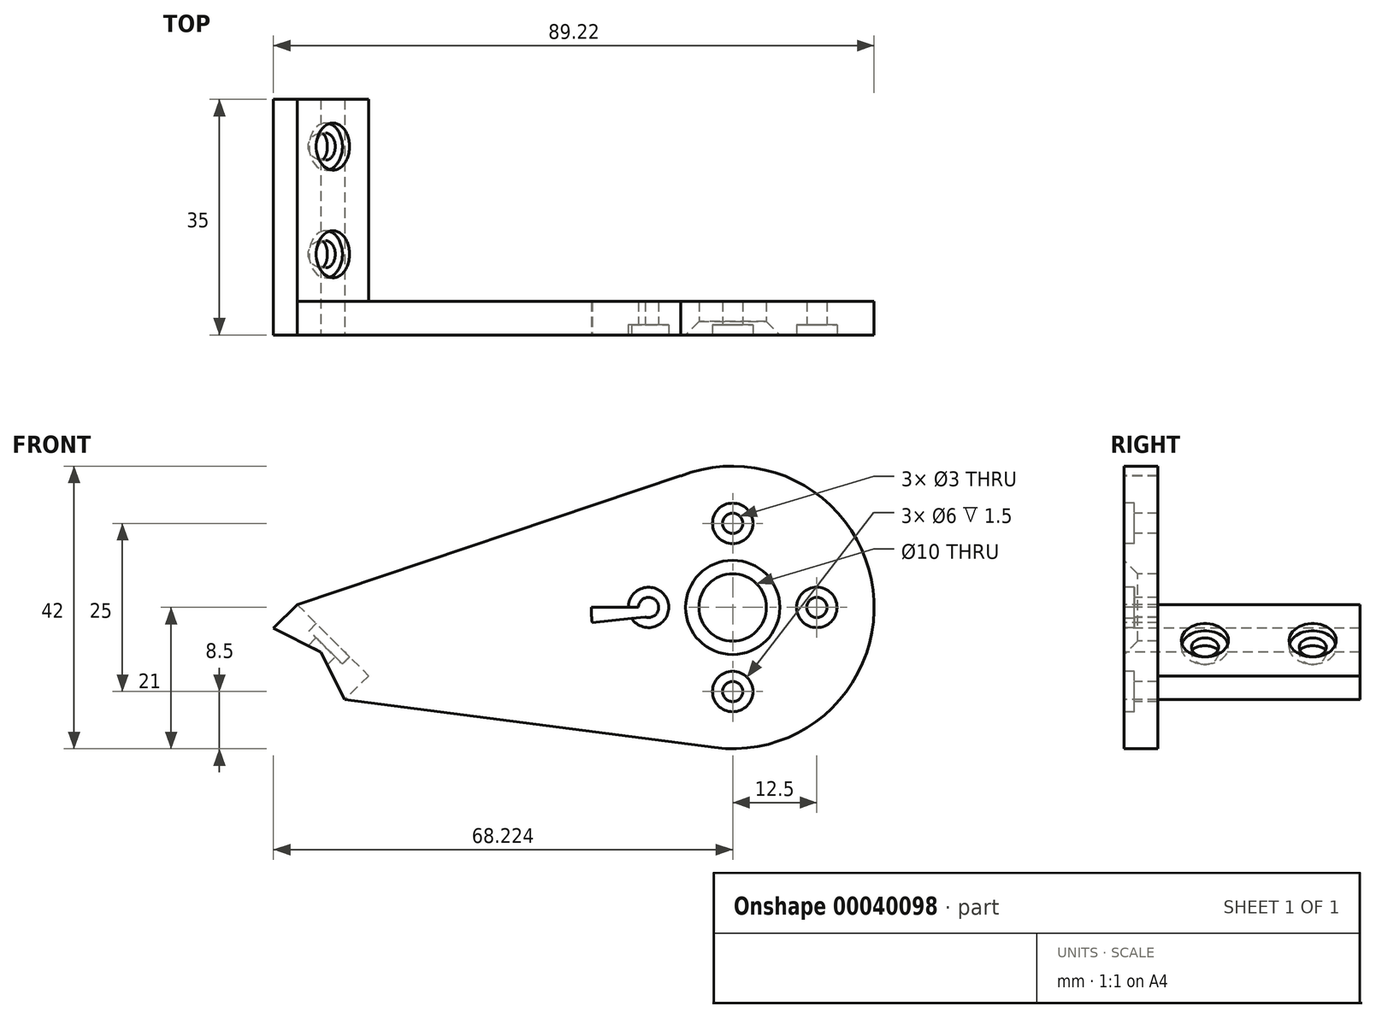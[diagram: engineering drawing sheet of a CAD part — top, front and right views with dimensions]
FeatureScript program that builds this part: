
annotation { "Feature Type Name" : "Feature", "Feature Type Description" : "" }
export const myFeature = defineFeature(function(context is Context, id is Id, definition is map)
    precondition{}
    {
        {
            var Q0;
            Q0=qCreatedBy(makeId("Front.planeOp"),FACE);
            var sketch = newSketch(context, id + "F0", { "sketchPlane" : qUnion([Q0])});
            skLineSegment(sketch, "E0", {"start": v(86.35, 0) * mm, "end": v(-90.04, 0) * mm});
            skLineSegment(sketch, "E1", {"start": v(-90.04, -43.67) * mm, "end": v(90.8, -43.67) * mm});
            skLineSegment(sketch, "E2", {"start": v(-90.04, 0) * mm, "end": v(-90.04, -43.67) * mm});
            skLineSegment(sketch, "E3", {"start": v(0, 0) * mm, "end": v(43.67, 0) * mm});
            skLineSegment(sketch, "E4", {"start": v(43.67, 0) * mm, "end": v(43.67, -43.67) * mm});
            skLineSegment(sketch, "E5", {"start": v(0, 0) * mm, "end": v(43.67, -43.67) * mm});
            skCircle(sketch, "E6", {"center": v(43.67, -43.67) * mm, "radius": 4 * mm});
            skLineSegment(sketch, "E7", {"start": v(40.84, -40.84) * mm, "end": v(37.39, -37.39) * mm});
            skLineSegment(sketch, "E8", {"start": v(37.39, -37.39) * mm, "end": v(43.67, -31.1) * mm});
            skLineSegment(sketch, "E9", {"start": v(37.39, -37.39) * mm, "end": v(31.1, -43.67) * mm});
            skLineSegment(sketch, "E10", {"start": v(31.1, -43.67) * mm, "end": v(41.7, -54.27) * mm});
            skLineSegment(sketch, "E11", {"start": v(43.67, -31.1) * mm, "end": v(54.27, -41.7) * mm});
            skArc(sketch, "E12", {"start": v(41.7, -54.27) * mm, "mid": v(51.29, -51.29) * mm, "end": v(54.27, -41.7) * mm});
            skCircle(sketch, "E13", {"center": v(43.67, -43.67) * mm, "radius": 31.25 * mm});
            skCircle(sketch, "E14", {"center": v(43.67, -43.67) * mm, "radius": 70 * mm});
            skLineSegment(sketch, "E15", {"start": v(86.35, 0) * mm, "end": v(86.35, -28) * mm});
            skLineSegment(sketch, "E16", {"start": v(86.35, -28) * mm, "end": v(135.4, -28) * mm});
            skCircle(sketch, "E17", {"center": v(111.9, -28) * mm, "radius": 21 * mm});
            skLineSegment(sketch, "E18", {"start": v(54.27, -41.7) * mm, "end": v(43.67, -31.1) * mm});
            skLineSegment(sketch, "E19", {"start": v(43.67, -31.1) * mm, "end": v(47.2, -27.57) * mm});
            skLineSegment(sketch, "E20", {"start": v(47.2, -27.57) * mm, "end": v(57.8, -38.17) * mm});
            skLineSegment(sketch, "E21", {"start": v(57.8, -38.17) * mm, "end": v(54.27, -41.7) * mm});
            skCircle(sketch, "E22", {"center": v(43.67, -43.67) * mm, "radius": 40 * mm});
            skLineSegment(sketch, "E23", {"start": v(47.2, -27.57) * mm, "end": v(54.27, -41.7) * mm});
            skLineSegment(sketch, "E24", {"start": v(43.67, -31.1) * mm, "end": v(57.8, -38.17) * mm});
            skLineSegment(sketch, "E25", {"start": v(-90.34, -83.67) * mm, "end": v(171.92, -83.67) * mm});
            skLineSegment(sketch, "E26", {"start": v(113.47, -48.94) * mm, "end": v(113.47, -83.67) * mm});
            skLineSegment(sketch, "E27", {"start": v(43.67, 0) * mm, "end": v(43.67, -3.67) * mm});
            skLineSegment(sketch, "E28", {"start": v(50.74, -34.64) * mm, "end": v(111.9, -28) * mm});
            skLineSegment(sketch, "E29", {"start": v(86.35, 0) * mm, "end": v(170.64, 0) * mm});
            skCircle(sketch, "E30", {"center": v(111.9, -28) * mm, "radius": 6 * mm});
            skCircle(sketch, "E31", {"center": v(111.9, -28) * mm, "radius": 12.5 * mm});
            skCircle(sketch, "E32", {"center": v(124.4, -28) * mm, "radius": 1.5 * mm});
            skCircle(sketch, "E33.1.0", {"center": v(111.9, -15.5) * mm, "radius": 1.5 * mm});
            skCircle(sketch, "E33.2.0", {"center": v(99.4, -28) * mm, "radius": 1.5 * mm});
            skCircle(sketch, "E33.3.0", {"center": v(111.9, -40.5) * mm, "radius": 1.5 * mm});
            skLineSegment(sketch, "E34", {"start": v(47.2, -27.57) * mm, "end": v(105.2, -8.1) * mm});
            skLineSegment(sketch, "E35", {"start": v(54.27, -41.7) * mm, "end": v(109.2, -48.83) * mm});
            skSolve(sketch);
        }
        {
            var Q0;
            {var subQ3=sQuery(id+"F0.wireOp",EDGE,"E19");Q0=makeQuery(id+"F0.imprint","IMPRINT",FACE,{"disambiguationData":[TD([[makeQuery(id+"F0.imprint","IMPRINT",EDGE,{"derivedFrom":subQ3}),-1.0]])]});}
            var Q1;
            {var subQ3=sQuery(id+"F0.wireOp",EDGE,"E18");Q1=makeQuery(id+"F0.imprint","IMPRINT",FACE,{"disambiguationData":[TD([[makeQuery(id+"F0.imprint","IMPRINT",EDGE,{"derivedFrom":subQ3}),-1.0]])]});}
            var Q2;
            {var subQ3=sQuery(id+"F0.wireOp",EDGE,"E21");Q2=makeQuery(id+"F0.imprint","IMPRINT",FACE,{"disambiguationData":[TD([[makeQuery(id+"F0.imprint","IMPRINT",EDGE,{"derivedFrom":subQ3}),-1.0]])]});}
            var Q3;
            {var subQ5=sQuery(id+"F0.wireOp",EDGE,"E21");Q3=makeQuery(id+"F0.imprint","IMPRINT",FACE,{"disambiguationData":[TD([[makeQuery(id+"F0.imprint","IMPRINT",EDGE,{"derivedFrom":subQ5}),1.0]])]});}
            var Q4;
            {var subQ1=sQuery(id+"F0.wireOp",EDGE,"E13");var subQ5=sQuery(id+"F0.wireOp",EDGE,"E28");var subQ7=makeQuery(id+"F0.imprint","INTERSECT",VERTEX,{"derivedFrom":[subQ1,subQ5]});Q4=makeQuery(id+"F0.imprint","IMPRINT",FACE,{"disambiguationData":[TD([[makeQuery(id+"F0.imprint","IMPRINT",EDGE,{"disambiguationData":[TD([[subQ7,-1.0]])],"derivedFrom":subQ1}),1.0]])]});}
            var Q5;
            {var subQ0=sQuery(id+"F0.wireOp",EDGE,"E28");var subQ1=sQuery(id+"F0.wireOp",EDGE,"E20");var subQ2=makeQuery(id+"F0.imprint","INTERSECT",VERTEX,{"derivedFrom":[subQ1,subQ0]});Q5=makeQuery(id+"F0.imprint","IMPRINT",FACE,{"disambiguationData":[TD([[makeQuery(id+"F0.imprint","IMPRINT",EDGE,{"disambiguationData":[TD([[subQ2,1.0]])],"derivedFrom":subQ0}),1.0]])]});}
            var Q6;
            {var subQ0=sQuery(id+"F0.wireOp",EDGE,"E28");var subQ1=sQuery(id+"F0.wireOp",EDGE,"E20");var subQ2=makeQuery(id+"F0.imprint","INTERSECT",VERTEX,{"derivedFrom":[subQ1,subQ0]});Q6=makeQuery(id+"F0.imprint","IMPRINT",FACE,{"disambiguationData":[TD([[makeQuery(id+"F0.imprint","IMPRINT",EDGE,{"disambiguationData":[TD([[subQ2,-1.0]])],"derivedFrom":subQ1}),-1.0]])]});}
            var Q7;
            {var subQ3=sQuery(id+"F0.wireOp",EDGE,"E13");var subQ5=sQuery(id+"F0.wireOp",EDGE,"E28");var subQ7=makeQuery(id+"F0.imprint","INTERSECT",VERTEX,{"derivedFrom":[subQ3,subQ5]});Q7=makeQuery(id+"F0.imprint","IMPRINT",FACE,{"disambiguationData":[TD([[makeQuery(id+"F0.imprint","IMPRINT",EDGE,{"disambiguationData":[TD([[subQ7,-1.0]])],"derivedFrom":subQ3}),-1.0]])]});}
            var Q8;
            {var subQ1=sQuery(id+"F0.wireOp",EDGE,"E22");var subQ5=sQuery(id+"F0.wireOp",EDGE,"E1");var subQ6=makeQuery(id+"F0.imprint","INTERSECT",VERTEX,{"disambiguationData":[OD(0.0)],"derivedFrom":[subQ5,subQ1]});Q8=makeQuery(id+"F0.imprint","IMPRINT",FACE,{"disambiguationData":[TD([[makeQuery(id+"F0.imprint","IMPRINT",EDGE,{"disambiguationData":[TD([[subQ6,1.0]])],"derivedFrom":subQ5}),1.0]])]});}
            var Q9;
            {var subQ0=sQuery(id+"F0.wireOp",EDGE,"E35");var subQ3=sQuery(id+"F0.wireOp",EDGE,"E17");var subQ4=makeQuery(id+"F0.imprint","INTERSECT",VERTEX,{"derivedFrom":[subQ3,subQ0]});Q9=makeQuery(id+"F0.imprint","IMPRINT",FACE,{"disambiguationData":[TD([[makeQuery(id+"F0.imprint","IMPRINT",EDGE,{"disambiguationData":[TD([[subQ4,1.0]])],"derivedFrom":subQ3}),-1.0]])]});}
            var Q10;
            {var subQ3=sQuery(id+"F0.wireOp",EDGE,"E15");var subQ9=sQuery(id+"F0.wireOp",EDGE,"E16");var subQ11=makeQuery(id+"F0.imprint","INTERSECT",VERTEX,{"derivedFrom":[subQ3,subQ9]});Q10=makeQuery(id+"F0.imprint","IMPRINT",FACE,{"disambiguationData":[TD([[makeQuery(id+"F0.imprint","IMPRINT",EDGE,{"disambiguationData":[TD([[subQ11,1.0]])],"derivedFrom":subQ3}),-1.0]])]});}
            var Q11;
            {var subQ0=sQuery(id+"F0.wireOp",EDGE,"E34");var subQ3=sQuery(id+"F0.wireOp",EDGE,"E14");var subQ4=makeQuery(id+"F0.imprint","INTERSECT",VERTEX,{"derivedFrom":[subQ3,subQ0]});Q11=makeQuery(id+"F0.imprint","IMPRINT",FACE,{"disambiguationData":[TD([[makeQuery(id+"F0.imprint","IMPRINT",EDGE,{"disambiguationData":[TD([[subQ4,1.0]])],"derivedFrom":subQ3}),1.0]])]});}
            var Q12;
            {var subQ1=sQuery(id+"F0.wireOp",EDGE,"E22");var subQ5=sQuery(id+"F0.wireOp",EDGE,"E1");var subQ6=makeQuery(id+"F0.imprint","INTERSECT",VERTEX,{"disambiguationData":[OD(0.0)],"derivedFrom":[subQ5,subQ1]});Q12=makeQuery(id+"F0.imprint","IMPRINT",FACE,{"disambiguationData":[TD([[makeQuery(id+"F0.imprint","IMPRINT",EDGE,{"disambiguationData":[TD([[subQ6,1.0]])],"derivedFrom":subQ5}),-1.0]])]});}
            var Q13;
            {var subQ0=sQuery(id+"F0.wireOp",EDGE,"E35");var subQ3=sQuery(id+"F0.wireOp",EDGE,"E1");var subQ4=makeQuery(id+"F0.imprint","INTERSECT",VERTEX,{"derivedFrom":[subQ3,subQ0]});Q13=makeQuery(id+"F0.imprint","IMPRINT",FACE,{"disambiguationData":[TD([[makeQuery(id+"F0.imprint","IMPRINT",EDGE,{"disambiguationData":[TD([[subQ4,-1.0]])],"derivedFrom":subQ3}),-1.0]])]});}
            var Q14;
            {var subQ0=sQuery(id+"F0.wireOp",EDGE,"E31");var subQ3=sQuery(id+"F0.wireOp",EDGE,"E14");var subQ4=makeQuery(id+"F0.imprint","INTERSECT",VERTEX,{"disambiguationData":[OD(1.0)],"derivedFrom":[subQ3,subQ0]});Q14=makeQuery(id+"F0.imprint","IMPRINT",FACE,{"disambiguationData":[TD([[makeQuery(id+"F0.imprint","IMPRINT",EDGE,{"disambiguationData":[TD([[subQ4,-1.0]])],"derivedFrom":subQ3}),1.0]])]});}
            var Q15;
            {var subQ5=sQuery(id+"F0.wireOp",EDGE,"E14");var subQ7=sQuery(id+"F0.wireOp",EDGE,"E30");var subQ9=makeQuery(id+"F0.imprint","INTERSECT",VERTEX,{"disambiguationData":[OD(1.0)],"derivedFrom":[subQ5,subQ7]});Q15=makeQuery(id+"F0.imprint","IMPRINT",FACE,{"disambiguationData":[TD([[makeQuery(id+"F0.imprint","IMPRINT",EDGE,{"disambiguationData":[TD([[subQ9,-1.0]])],"derivedFrom":subQ5}),1.0]])]});}
            var Q16;
            {var subQ8=sQuery(id+"F0.wireOp",EDGE,"E14");var subQ10=sQuery(id+"F0.wireOp",EDGE,"E30");var subQ12=makeQuery(id+"F0.imprint","INTERSECT",VERTEX,{"disambiguationData":[OD(1.0)],"derivedFrom":[subQ8,subQ10]});Q16=makeQuery(id+"F0.imprint","IMPRINT",FACE,{"disambiguationData":[TD([[makeQuery(id+"F0.imprint","IMPRINT",EDGE,{"disambiguationData":[TD([[subQ12,-1.0]])],"derivedFrom":subQ8}),-1.0]])]});}
            var Q17;
            {var subQ1=sQuery(id+"F0.wireOp",EDGE,"E31");var subQ8=sQuery(id+"F0.wireOp",EDGE,"E14");var subQ9=makeQuery(id+"F0.imprint","INTERSECT",VERTEX,{"disambiguationData":[OD(1.0)],"derivedFrom":[subQ8,subQ1]});Q17=makeQuery(id+"F0.imprint","IMPRINT",FACE,{"disambiguationData":[TD([[makeQuery(id+"F0.imprint","IMPRINT",EDGE,{"disambiguationData":[TD([[subQ9,-1.0]])],"derivedFrom":subQ8}),-1.0]])]});}
            var Q18;
            {var subQ3=sQuery(id+"F0.wireOp",EDGE,"E16");var subQ7=sQuery(id+"F0.wireOp",EDGE,"E17");var subQ8=makeQuery(id+"F0.imprint","INTERSECT",VERTEX,{"disambiguationData":[OD(0.0)],"derivedFrom":[subQ3,subQ7]});Q18=makeQuery(id+"F0.imprint","IMPRINT",FACE,{"disambiguationData":[TD([[makeQuery(id+"F0.imprint","IMPRINT",EDGE,{"disambiguationData":[TD([[subQ8,1.0]])],"derivedFrom":subQ3}),-1.0]])]});}
            var Q19;
            {var subQ5=sQuery(id+"F0.wireOp",EDGE,"E30");var subQ7=sQuery(id+"F0.wireOp",EDGE,"E14");var subQ8=makeQuery(id+"F0.imprint","INTERSECT",VERTEX,{"disambiguationData":[OD(0.0)],"derivedFrom":[subQ7,subQ5]});Q19=makeQuery(id+"F0.imprint","IMPRINT",FACE,{"disambiguationData":[TD([[makeQuery(id+"F0.imprint","IMPRINT",EDGE,{"disambiguationData":[TD([[subQ8,1.0]])],"derivedFrom":subQ7}),-1.0]])]});}
            var Q20;
            {var subQ8=sQuery(id+"F0.wireOp",EDGE,"E14");var subQ10=sQuery(id+"F0.wireOp",EDGE,"E30");var subQ12=makeQuery(id+"F0.imprint","INTERSECT",VERTEX,{"disambiguationData":[OD(0.0)],"derivedFrom":[subQ8,subQ10]});Q20=makeQuery(id+"F0.imprint","IMPRINT",FACE,{"disambiguationData":[TD([[makeQuery(id+"F0.imprint","IMPRINT",EDGE,{"disambiguationData":[TD([[subQ12,1.0]])],"derivedFrom":subQ8}),1.0]])]});}
            var Q21;
            {var subQ9=sQuery(id+"F0.wireOp",EDGE,"E17");var subQ11=makeQuery(id+"F0.imprint","INTERSECT",VERTEX,{"derivedFrom":[subQ9,sQuery(id+"F0.wireOp",EDGE,"E35")]});Q21=makeQuery(id+"F0.imprint","IMPRINT",FACE,{"disambiguationData":[TD([[makeQuery(id+"F0.imprint","IMPRINT",EDGE,{"disambiguationData":[TD([[subQ11,1.0]])],"derivedFrom":subQ9}),1.0]])]});}
            var Q22;
            {var subQ3=sQuery(id+"F0.wireOp",EDGE,"E16");var subQ5=sQuery(id+"F0.wireOp",EDGE,"E17");var subQ7=makeQuery(id+"F0.imprint","INTERSECT",VERTEX,{"disambiguationData":[OD(1.0)],"derivedFrom":[subQ3,subQ5]});Q22=makeQuery(id+"F0.imprint","IMPRINT",FACE,{"disambiguationData":[TD([[makeQuery(id+"F0.imprint","IMPRINT",EDGE,{"disambiguationData":[TD([[subQ7,-1.0]])],"derivedFrom":subQ3}),-1.0]])]});}
            var Q23;
            {var subQ0=sQuery(id+"F0.wireOp",EDGE,"E33.2.0");var subQ3=sQuery(id+"F0.wireOp",EDGE,"E16");var subQ4=makeQuery(id+"F0.imprint","INTERSECT",VERTEX,{"disambiguationData":[OD(1.0)],"derivedFrom":[subQ3,subQ0]});Q23=makeQuery(id+"F0.imprint","IMPRINT",FACE,{"disambiguationData":[TD([[makeQuery(id+"F0.imprint","IMPRINT",EDGE,{"disambiguationData":[TD([[subQ4,-1.0]])],"derivedFrom":subQ3}),-1.0]])]});}
            var Q24;
            {var subQ0=sQuery(id+"F0.wireOp",EDGE,"E30");var subQ3=sQuery(id+"F0.wireOp",EDGE,"E14");var subQ4=makeQuery(id+"F0.imprint","INTERSECT",VERTEX,{"disambiguationData":[OD(0.0)],"derivedFrom":[subQ3,subQ0]});Q24=makeQuery(id+"F0.imprint","IMPRINT",FACE,{"disambiguationData":[TD([[makeQuery(id+"F0.imprint","IMPRINT",EDGE,{"disambiguationData":[TD([[subQ4,1.0]])],"derivedFrom":subQ0}),1.0]])]});}
            var Q25;
            {var subQ0=sQuery(id+"F0.wireOp",EDGE,"E30");var subQ3=sQuery(id+"F0.wireOp",EDGE,"E14");var subQ4=makeQuery(id+"F0.imprint","INTERSECT",VERTEX,{"disambiguationData":[OD(0.0)],"derivedFrom":[subQ3,subQ0]});Q25=makeQuery(id+"F0.imprint","IMPRINT",FACE,{"disambiguationData":[TD([[makeQuery(id+"F0.imprint","IMPRINT",EDGE,{"disambiguationData":[TD([[subQ4,-1.0]])],"derivedFrom":subQ0}),1.0]])]});}
            var Q26;
            {var subQ0=sQuery(id+"F0.wireOp",EDGE,"E30");var subQ3=sQuery(id+"F0.wireOp",EDGE,"E14");var subQ4=makeQuery(id+"F0.imprint","INTERSECT",VERTEX,{"disambiguationData":[OD(1.0)],"derivedFrom":[subQ3,subQ0]});Q26=makeQuery(id+"F0.imprint","IMPRINT",FACE,{"disambiguationData":[TD([[makeQuery(id+"F0.imprint","IMPRINT",EDGE,{"disambiguationData":[TD([[subQ4,1.0]])],"derivedFrom":subQ0}),1.0]])]});}
            var Q27;
            {var subQ0=sQuery(id+"F0.wireOp",EDGE,"E30");var subQ3=sQuery(id+"F0.wireOp",EDGE,"E14");var subQ4=makeQuery(id+"F0.imprint","INTERSECT",VERTEX,{"disambiguationData":[OD(1.0)],"derivedFrom":[subQ3,subQ0]});Q27=makeQuery(id+"F0.imprint","IMPRINT",FACE,{"disambiguationData":[TD([[makeQuery(id+"F0.imprint","IMPRINT",EDGE,{"disambiguationData":[TD([[subQ4,-1.0]])],"derivedFrom":subQ0}),1.0]])]});}
            var Q28;
            {var subQ0=sQuery(id+"F0.wireOp",EDGE,"E30");var subQ3=sQuery(id+"F0.wireOp",EDGE,"E16");var subQ4=makeQuery(id+"F0.imprint","INTERSECT",VERTEX,{"disambiguationData":[OD(0.0)],"derivedFrom":[subQ3,subQ0]});Q28=makeQuery(id+"F0.imprint","IMPRINT",FACE,{"disambiguationData":[TD([[makeQuery(id+"F0.imprint","IMPRINT",EDGE,{"disambiguationData":[TD([[subQ4,-1.0]])],"derivedFrom":subQ0}),1.0]])]});}
            var Q29;
            {var subQ0=sQuery(id+"F0.wireOp",EDGE,"E33.2.0");var subQ3=sQuery(id+"F0.wireOp",EDGE,"E16");var subQ4=makeQuery(id+"F0.imprint","INTERSECT",VERTEX,{"disambiguationData":[OD(0.0)],"derivedFrom":[subQ3,subQ0]});Q29=makeQuery(id+"F0.imprint","IMPRINT",FACE,{"disambiguationData":[TD([[makeQuery(id+"F0.imprint","IMPRINT",EDGE,{"disambiguationData":[TD([[subQ4,-1.0]])],"derivedFrom":subQ3}),-1.0]])]});}
            var Q30;
            {var subQ0=sQuery(id+"F0.wireOp",EDGE,"E33.2.0");var subQ3=sQuery(id+"F0.wireOp",EDGE,"E16");var subQ4=makeQuery(id+"F0.imprint","INTERSECT",VERTEX,{"disambiguationData":[OD(0.0)],"derivedFrom":[subQ3,subQ0]});Q30=makeQuery(id+"F0.imprint","IMPRINT",FACE,{"disambiguationData":[TD([[makeQuery(id+"F0.imprint","IMPRINT",EDGE,{"disambiguationData":[TD([[subQ4,-1.0]])],"derivedFrom":subQ3}),1.0]])]});}
            var Q31;
            {var subQ1=sQuery(id+"F0.wireOp",EDGE,"E31");var subQ3=sQuery(id+"F0.wireOp",EDGE,"E16");var subQ5=makeQuery(id+"F0.imprint","INTERSECT",VERTEX,{"disambiguationData":[OD(0.0)],"derivedFrom":[subQ3,subQ1]});Q31=makeQuery(id+"F0.imprint","IMPRINT",FACE,{"disambiguationData":[TD([[makeQuery(id+"F0.imprint","IMPRINT",EDGE,{"disambiguationData":[TD([[subQ5,-1.0]])],"derivedFrom":subQ3}),1.0]])]});}
            var Q32;
            {var subQ3=sQuery(id+"F0.wireOp",EDGE,"E16");var subQ5=sQuery(id+"F0.wireOp",EDGE,"E31");var subQ7=makeQuery(id+"F0.imprint","INTERSECT",VERTEX,{"disambiguationData":[OD(0.0)],"derivedFrom":[subQ3,subQ5]});Q32=makeQuery(id+"F0.imprint","IMPRINT",FACE,{"disambiguationData":[TD([[makeQuery(id+"F0.imprint","IMPRINT",EDGE,{"disambiguationData":[TD([[subQ7,-1.0]])],"derivedFrom":subQ3}),-1.0]])]});}
            var Q33;
            {var subQ0=sQuery(id+"F0.wireOp",EDGE,"E33.2.0");var subQ3=sQuery(id+"F0.wireOp",EDGE,"E28");var subQ4=makeQuery(id+"F0.imprint","INTERSECT",VERTEX,{"disambiguationData":[OD(0.0)],"derivedFrom":[subQ3,subQ0]});Q33=makeQuery(id+"F0.imprint","IMPRINT",FACE,{"disambiguationData":[TD([[makeQuery(id+"F0.imprint","IMPRINT",EDGE,{"disambiguationData":[TD([[subQ4,-1.0]])],"derivedFrom":subQ3}),-1.0]])]});}
            var Q34;
            {var subQ1=sQuery(id+"F0.wireOp",EDGE,"E31");var subQ3=sQuery(id+"F0.wireOp",EDGE,"E28");var subQ5=makeQuery(id+"F0.imprint","INTERSECT",VERTEX,{"derivedFrom":[subQ3,subQ1]});Q34=makeQuery(id+"F0.imprint","IMPRINT",FACE,{"disambiguationData":[TD([[makeQuery(id+"F0.imprint","IMPRINT",EDGE,{"disambiguationData":[TD([[subQ5,-1.0]])],"derivedFrom":subQ3}),-1.0]])]});}
            var Q35;
            {var subQ0=sQuery(id+"F0.wireOp",EDGE,"E33.3.0");var subQ1=sQuery(id+"F0.wireOp",EDGE,"E31");var subQ3=makeQuery(id+"F0.imprint","INTERSECT",VERTEX,{"disambiguationData":[OD(0.0)],"derivedFrom":[subQ1,subQ0]});Q35=makeQuery(id+"F0.imprint","IMPRINT",FACE,{"disambiguationData":[TD([[makeQuery(id+"F0.imprint","IMPRINT",EDGE,{"disambiguationData":[TD([[subQ3,-1.0]])],"derivedFrom":subQ1}),1.0]])]});}
            var Q36;
            {var subQ0=sQuery(id+"F0.wireOp",EDGE,"E33.3.0");var subQ1=sQuery(id+"F0.wireOp",EDGE,"E31");var subQ3=makeQuery(id+"F0.imprint","INTERSECT",VERTEX,{"disambiguationData":[OD(0.0)],"derivedFrom":[subQ1,subQ0]});Q36=makeQuery(id+"F0.imprint","IMPRINT",FACE,{"disambiguationData":[TD([[makeQuery(id+"F0.imprint","IMPRINT",EDGE,{"disambiguationData":[TD([[subQ3,-1.0]])],"derivedFrom":subQ1}),-1.0]])]});}
            var Q37;
            {var subQ1=sQuery(id+"F0.wireOp",EDGE,"E31");var subQ3=sQuery(id+"F0.wireOp",EDGE,"E16");var subQ5=makeQuery(id+"F0.imprint","INTERSECT",VERTEX,{"disambiguationData":[OD(1.0)],"derivedFrom":[subQ3,subQ1]});Q37=makeQuery(id+"F0.imprint","IMPRINT",FACE,{"disambiguationData":[TD([[makeQuery(id+"F0.imprint","IMPRINT",EDGE,{"disambiguationData":[TD([[subQ5,-1.0]])],"derivedFrom":subQ3}),-1.0]])]});}
            var Q38;
            {var subQ0=sQuery(id+"F0.wireOp",EDGE,"E32");var subQ3=sQuery(id+"F0.wireOp",EDGE,"E16");var subQ4=makeQuery(id+"F0.imprint","INTERSECT",VERTEX,{"disambiguationData":[OD(0.0)],"derivedFrom":[subQ3,subQ0]});Q38=makeQuery(id+"F0.imprint","IMPRINT",FACE,{"disambiguationData":[TD([[makeQuery(id+"F0.imprint","IMPRINT",EDGE,{"disambiguationData":[TD([[subQ4,-1.0]])],"derivedFrom":subQ3}),-1.0]])]});}
            var Q39;
            {var subQ0=sQuery(id+"F0.wireOp",EDGE,"E32");var subQ3=sQuery(id+"F0.wireOp",EDGE,"E16");var subQ4=makeQuery(id+"F0.imprint","INTERSECT",VERTEX,{"disambiguationData":[OD(0.0)],"derivedFrom":[subQ3,subQ0]});Q39=makeQuery(id+"F0.imprint","IMPRINT",FACE,{"disambiguationData":[TD([[makeQuery(id+"F0.imprint","IMPRINT",EDGE,{"disambiguationData":[TD([[subQ4,-1.0]])],"derivedFrom":subQ3}),1.0]])]});}
            var Q40;
            {var subQ1=sQuery(id+"F0.wireOp",EDGE,"E31");var subQ3=sQuery(id+"F0.wireOp",EDGE,"E16");var subQ5=makeQuery(id+"F0.imprint","INTERSECT",VERTEX,{"disambiguationData":[OD(1.0)],"derivedFrom":[subQ3,subQ1]});Q40=makeQuery(id+"F0.imprint","IMPRINT",FACE,{"disambiguationData":[TD([[makeQuery(id+"F0.imprint","IMPRINT",EDGE,{"disambiguationData":[TD([[subQ5,-1.0]])],"derivedFrom":subQ3}),1.0]])]});}
            var Q41;
            {var subQ0=sQuery(id+"F0.wireOp",EDGE,"E33.1.0");var subQ1=sQuery(id+"F0.wireOp",EDGE,"E31");var subQ3=makeQuery(id+"F0.imprint","INTERSECT",VERTEX,{"disambiguationData":[OD(0.0)],"derivedFrom":[subQ1,subQ0]});Q41=makeQuery(id+"F0.imprint","IMPRINT",FACE,{"disambiguationData":[TD([[makeQuery(id+"F0.imprint","IMPRINT",EDGE,{"disambiguationData":[TD([[subQ3,-1.0]])],"derivedFrom":subQ1}),1.0]])]});}
            var Q42;
            {var subQ0=sQuery(id+"F0.wireOp",EDGE,"E33.1.0");var subQ1=sQuery(id+"F0.wireOp",EDGE,"E31");var subQ3=makeQuery(id+"F0.imprint","INTERSECT",VERTEX,{"disambiguationData":[OD(0.0)],"derivedFrom":[subQ1,subQ0]});Q42=makeQuery(id+"F0.imprint","IMPRINT",FACE,{"disambiguationData":[TD([[makeQuery(id+"F0.imprint","IMPRINT",EDGE,{"disambiguationData":[TD([[subQ3,-1.0]])],"derivedFrom":subQ1}),-1.0]])]});}
            extrude(context, id + "F1", {"entities" : qUnion([Q0, Q1, Q2, Q3, Q4, Q5, Q6, Q7, Q8, Q9, Q10, Q11, Q12, Q13, Q14, Q15, Q16, Q17, Q18, Q19, Q20, Q21, Q22, Q23, Q24, Q25, Q26, Q27, Q28, Q29, Q30, Q31, Q32, Q33, Q34, Q35, Q36, Q37, Q38, Q39, Q40, Q41, Q42]), "oppositeDirection" : true, "depth" : 5 * mm});
        }
        {
            var Q0;
            {var subQ3=sQuery(id+"F0.wireOp",EDGE,"E19");Q0=makeQuery(id+"F0.imprint","IMPRINT",FACE,{"disambiguationData":[TD([[makeQuery(id+"F0.imprint","IMPRINT",EDGE,{"derivedFrom":subQ3}),-1.0]])]});}
            var Q1;
            {var subQ3=sQuery(id+"F0.wireOp",EDGE,"E18");Q1=makeQuery(id+"F0.imprint","IMPRINT",FACE,{"disambiguationData":[TD([[makeQuery(id+"F0.imprint","IMPRINT",EDGE,{"derivedFrom":subQ3}),-1.0]])]});}
            var Q2;
            {var subQ3=sQuery(id+"F0.wireOp",EDGE,"E21");Q2=makeQuery(id+"F0.imprint","IMPRINT",FACE,{"disambiguationData":[TD([[makeQuery(id+"F0.imprint","IMPRINT",EDGE,{"derivedFrom":subQ3}),-1.0]])]});}
            var Q3;
            {var subQ0=sQuery(id+"F0.wireOp",EDGE,"E28");var subQ1=sQuery(id+"F0.wireOp",EDGE,"E20");var subQ2=makeQuery(id+"F0.imprint","INTERSECT",VERTEX,{"derivedFrom":[subQ1,subQ0]});Q3=makeQuery(id+"F0.imprint","IMPRINT",FACE,{"disambiguationData":[TD([[makeQuery(id+"F0.imprint","IMPRINT",EDGE,{"disambiguationData":[TD([[subQ2,-1.0]])],"derivedFrom":subQ1}),-1.0]])]});}
            var Q4;
            {var subQ0=sQuery(id+"F0.wireOp",EDGE,"E28");var subQ1=sQuery(id+"F0.wireOp",EDGE,"E20");var subQ2=makeQuery(id+"F0.imprint","INTERSECT",VERTEX,{"derivedFrom":[subQ1,subQ0]});Q4=makeQuery(id+"F0.imprint","IMPRINT",FACE,{"disambiguationData":[TD([[makeQuery(id+"F0.imprint","IMPRINT",EDGE,{"disambiguationData":[TD([[subQ2,1.0]])],"derivedFrom":subQ0}),1.0]])]});}
            extrude(context, id + "F2", {"entities" : qUnion([Q0, Q1, Q2, Q3, Q4]), "operationType" : NewBodyOperationType.ADD, "oppositeDirection" : true, "depth" : 35 * mm});
        }
        {
            var Q0;
            Q0=sQuery(id+"F0.wireOp",VERTEX,"E33.1.0.center");
            var Q1;
            Q1=sQuery(id+"F0.wireOp",VERTEX,"E32.center");
            var Q2;
            Q2=sQuery(id+"F0.wireOp",VERTEX,"E33.3.0.center");
            var Q3;
            Q3=sQuery(id+"F0.wireOp",VERTEX,"E33.2.0.center");
            var Q4;
            Q4=makeQuery(id+"F1.opExtrude","SWEPT_BODY",BODY,{"disambiguationData":[OSD([sQuery(id+"F0.wireOp",EDGE,"E14"),sQuery(id+"F0.wireOp",EDGE,"E17"),sQuery(id+"F0.wireOp",EDGE,"E18"),sQuery(id+"F0.wireOp",EDGE,"E19"),sQuery(id+"F0.wireOp",EDGE,"E34"),sQuery(id+"F0.wireOp",EDGE,"E35")])]});
            hole(context, id + "F3", {"style" : HoleStyle.C_BORE, "holeDiameter" : 3 * mm, "cBoreDiameter" : 6 * mm, "cBoreDepth" : 1.5 * mm, "endStyle" : HoleEndStyle.THROUGH, "locations" : qUnion([Q0, Q1, Q2, Q3]), "scope" : qUnion([Q4])});
        }
        {
            var Q0;
            Q0=sQuery(id+"F0.wireOp",VERTEX,"E17.center");
            var Q1;
            Q1=makeQuery(id+"F1.opExtrude","SWEPT_BODY",BODY,{"disambiguationData":[OSD([sQuery(id+"F0.wireOp",EDGE,"E14"),sQuery(id+"F0.wireOp",EDGE,"E17"),sQuery(id+"F0.wireOp",EDGE,"E18"),sQuery(id+"F0.wireOp",EDGE,"E19"),sQuery(id+"F0.wireOp",EDGE,"E34"),sQuery(id+"F0.wireOp",EDGE,"E35")])]});
            hole(context, id + "F4", {"style" : HoleStyle.C_SINK, "holeDiameter" : 10 * mm, "cSinkDiameter" : 14 * mm, "endStyle" : HoleEndStyle.THROUGH, "locations" : qUnion([Q0]), "scope" : qUnion([Q1]), "cSinkAngle" : 90 * degree});
        }
        {
            var Q0;
            Q0=makeQuery(id+"F2.opExtrude","SWEPT_FACE",FACE,{"disambiguationData":[OSD([sQuery(id+"F0.wireOp",EDGE,"E20")])]});
            var sketch = newSketch(context, id + "F5", { "sketchPlane" : qUnion([Q0])});
            skLineSegment(sketch, "E36", {"start": v(5, -52.88) * mm, "end": v(35, -52.88) * mm});
            skLineSegment(sketch, "E37", {"start": v(35, -52.88) * mm, "end": v(35, -67.87) * mm});
            skLineSegment(sketch, "E38", {"start": v(35, -67.87) * mm, "end": v(5, -67.87) * mm});
            skLineSegment(sketch, "E39", {"start": v(5, -67.87) * mm, "end": v(5, -52.88) * mm});
            skLineSegment(sketch, "E40", {"start": v(35, -52.88) * mm, "end": v(35, -60.37) * mm});
            skLineSegment(sketch, "E41", {"start": v(35, -60.37) * mm, "end": v(5, -60.37) * mm});
            skCircle(sketch, "E42", {"center": v(28, -60.37) * mm, "radius": 2 * mm});
            skCircle(sketch, "E43", {"center": v(12, -60.37) * mm, "radius": 2 * mm});
            skLineSegment(sketch, "E44", {"start": v(28, -60.37) * mm, "end": v(35, -60.37) * mm});
            skLineSegment(sketch, "E45", {"start": v(12, -60.37) * mm, "end": v(5, -60.37) * mm});
            skSolve(sketch);
        }
        {
            var Q0;
            Q0=sQuery(id+"F5.wireOp",VERTEX,"E42.center");
            var Q1;
            Q1=sQuery(id+"F5.wireOp",VERTEX,"E45.start");
            var Q2;
            Q2=makeQuery(id+"F1.opExtrude","SWEPT_BODY",BODY,{"disambiguationData":[OSD([sQuery(id+"F0.wireOp",EDGE,"E14"),sQuery(id+"F0.wireOp",EDGE,"E17"),sQuery(id+"F0.wireOp",EDGE,"E18"),sQuery(id+"F0.wireOp",EDGE,"E19"),sQuery(id+"F0.wireOp",EDGE,"E34"),sQuery(id+"F0.wireOp",EDGE,"E35")])]});
            hole(context, id + "F6", {"style" : HoleStyle.C_BORE, "holeDiameter" : 4 * mm, "cBoreDiameter" : 7 * mm, "cBoreDepth" : 1.5 * mm, "endStyle" : HoleEndStyle.THROUGH, "locations" : qUnion([Q0, Q1]), "scope" : qUnion([Q2])});
        }
    });
